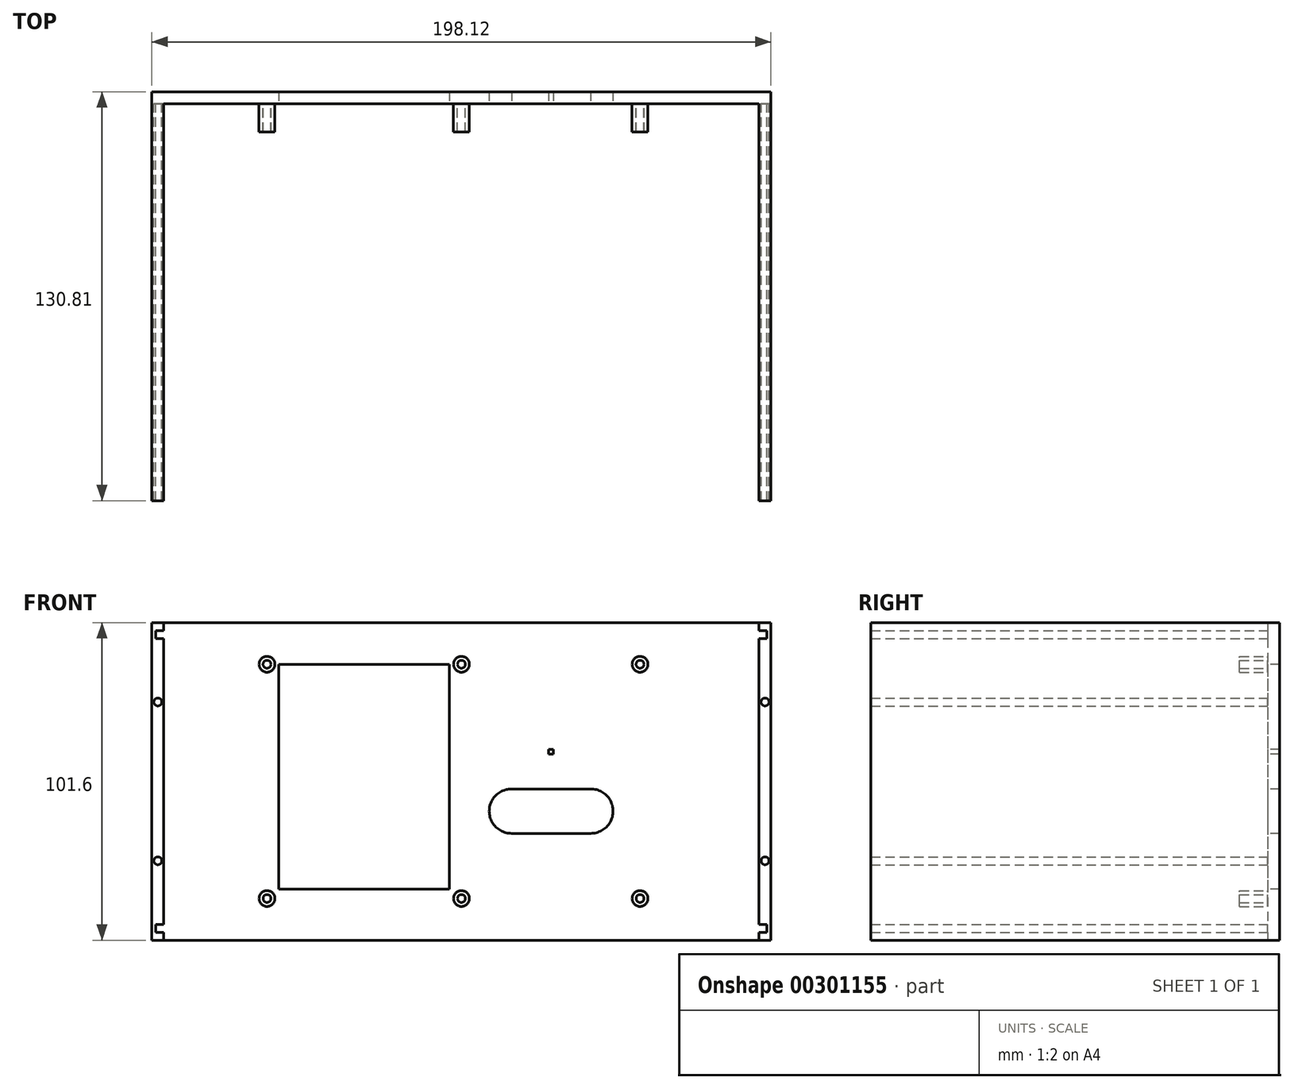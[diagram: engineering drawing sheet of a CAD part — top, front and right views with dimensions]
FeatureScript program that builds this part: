
annotation { "Feature Type Name" : "Feature", "Feature Type Description" : "" }
export const myFeature = defineFeature(function(context is Context, id is Id, definition is map)
    precondition{}
    {
        {
            var Q0;
            Q0=qCreatedBy(makeId("Front.planeOp"),FACE);
            var sketch = newSketch(context, id + "F0", { "sketchPlane" : qUnion([Q0])});
            skLineSegment(sketch, "E0.bottom", {"start": v(99.06, 50.8) * mm, "end": v(-99.06, 50.8) * mm});
            skLineSegment(sketch, "E0.top", {"start": v(99.06, -50.8) * mm, "end": v(-99.06, -50.8) * mm});
            skLineSegment(sketch, "E0.left", {"start": v(99.06, 50.8) * mm, "end": v(99.06, -50.8) * mm});
            skLineSegment(sketch, "E0.right", {"start": v(-99.06, 50.8) * mm, "end": v(-99.06, -50.8) * mm});
            skPoint(sketch, "E0.middle", {"position": v(0, 0) * mm});
            skSolve(sketch);
        }
        {
            var Q0;
            Q0=qCreatedBy(makeId("Front.planeOp"),FACE);
            var sketch = newSketch(context, id + "F1", { "sketchPlane" : qUnion([Q0])});
            skCircle(sketch, "E1", {"center": v(-62.23, -37.47) * mm, "radius": 2.54 * mm});
            skCircle(sketch, "E2", {"center": v(-62.23, 37.47) * mm, "radius": 2.54 * mm});
            skCircle(sketch, "E3", {"center": v(0, 37.47) * mm, "radius": 2.54 * mm});
            skCircle(sketch, "E4", {"center": v(0, -37.46) * mm, "radius": 2.54 * mm});
            skCircle(sketch, "E5", {"center": v(57.15, -37.46) * mm, "radius": 2.54 * mm});
            skCircle(sketch, "E6", {"center": v(57.15, 37.47) * mm, "radius": 2.54 * mm});
            skSolve(sketch);
        }
        {
            var Q0;
            Q0 = qSketchRegion(id + "F0", true);
            extrude(context, id + "F2", {"entities" : qUnion([Q0]), "depth" : 3.8 * mm});
        }
        {
            var Q0;
            Q0 = qSketchRegion(id + "F1", true);
            extrude(context, id + "F3", {"entities" : qUnion([Q0]), "operationType" : NewBodyOperationType.ADD, "depth" : 12.88 * mm});
        }
        {
            var Q0;
            Q0=makeQuery(id+"F2.opExtrude","CAP_FACE",FACE,{"disambiguationData":[OSD([sQuery(id+"F0.wireOp",EDGE,"E0.bottom"),sQuery(id+"F0.wireOp",EDGE,"E0.top"),sQuery(id+"F0.wireOp",EDGE,"E0.left"),sQuery(id+"F0.wireOp",EDGE,"E0.right")])],"isStart":false});
            var sketch = newSketch(context, id + "F4", { "sketchPlane" : qUnion([Q0])});
            skCircle(sketch, "E7", {"center": v(-62.23, 37.47) * mm, "radius": 1.27 * mm});
            skCircle(sketch, "E8", {"center": v(-62.23, -37.47) * mm, "radius": 1.26 * mm});
            skCircle(sketch, "E9", {"center": v(57.15, -37.46) * mm, "radius": 1.27 * mm});
            skCircle(sketch, "E10", {"center": v(57.15, 37.47) * mm, "radius": 1.27 * mm});
            skCircle(sketch, "E11", {"center": v(0, -37.46) * mm, "radius": 1.27 * mm});
            skCircle(sketch, "E12", {"center": v(0, 37.47) * mm, "radius": 1.26 * mm});
            skSolve(sketch);
        }
        {
            var Q0;
            Q0 = qSketchRegion(id + "F4", true);
            extrude(context, id + "F5", {"entities" : qUnion([Q0]), "operationType" : NewBodyOperationType.REMOVE, "depth" : 10.34 * mm});
        }
        {
            var Q0;
            Q0=makeQuery(id+"F2.opExtrude","CAP_FACE",FACE,{"disambiguationData":[OSD([sQuery(id+"F0.wireOp",EDGE,"E0.bottom"),sQuery(id+"F0.wireOp",EDGE,"E0.top"),sQuery(id+"F0.wireOp",EDGE,"E0.left"),sQuery(id+"F0.wireOp",EDGE,"E0.right")])],"isStart":false});
            var sketch = newSketch(context, id + "F6", { "sketchPlane" : qUnion([Q0])});
            skLineSegment(sketch, "E13.bottom", {"start": v(-58.42, 37.47) * mm, "end": v(-3.81, 37.47) * mm});
            skLineSegment(sketch, "E13.top", {"start": v(-58.42, -34.42) * mm, "end": v(-3.8, -34.42) * mm});
            skLineSegment(sketch, "E13.left", {"start": v(-58.42, 37.47) * mm, "end": v(-58.42, -34.42) * mm});
            skLineSegment(sketch, "E13.right", {"start": v(-3.81, 37.47) * mm, "end": v(-3.8, -34.42) * mm});
            skCircle(sketch, "E14", {"center": v(16, -9.52) * mm, "radius": 7.11 * mm});
            skCircle(sketch, "E15", {"center": v(41.4, -9.52) * mm, "radius": 7.11 * mm});
            skLineSegment(sketch, "E16.bottom", {"start": v(15.95, -2.41) * mm, "end": v(41.32, -2.41) * mm});
            skLineSegment(sketch, "E16.top", {"start": v(15.95, -16.64) * mm, "end": v(41.32, -16.64) * mm});
            skLineSegment(sketch, "E16.left", {"start": v(15.95, -2.41) * mm, "end": v(15.95, -16.64) * mm});
            skLineSegment(sketch, "E16.right", {"start": v(41.32, -2.41) * mm, "end": v(41.32, -16.64) * mm});
            skLineSegment(sketch, "E17.bottom", {"start": v(27.94, 10.29) * mm, "end": v(29.46, 10.29) * mm});
            skLineSegment(sketch, "E17.top", {"start": v(27.94, 8.76) * mm, "end": v(29.46, 8.76) * mm});
            skLineSegment(sketch, "E17.left", {"start": v(27.94, 10.29) * mm, "end": v(27.94, 8.76) * mm});
            skLineSegment(sketch, "E17.right", {"start": v(29.46, 10.29) * mm, "end": v(29.46, 8.76) * mm});
            skSolve(sketch);
        }
        {
            var Q0;
            Q0=makeQuery(id+"F6.imprint","IMPRINT",FACE,{"disambiguationData":[TD([[makeQuery(id+"F6.imprint","IMPRINT",EDGE,{"derivedFrom":sQuery(id+"F6.wireOp",EDGE,"E13.bottom")}),-1.0]])]});
            var Q1;
            Q1=makeQuery(id+"F6.imprint","IMPRINT",FACE,{"disambiguationData":[TD([[makeQuery(id+"F6.imprint","IMPRINT",EDGE,{"derivedFrom":sQuery(id+"F6.wireOp",EDGE,"E14")}),1.0]])]});
            var Q2;
            Q2=makeQuery(id+"F6.imprint","IMPRINT",FACE,{"disambiguationData":[TD([[makeQuery(id+"F6.imprint","IMPRINT",EDGE,{"derivedFrom":sQuery(id+"F6.wireOp",EDGE,"E15")}),1.0]])]});
            var Q3;
            {var subQ1=sQuery(id+"F6.wireOp",EDGE,"E16.bottom");var subQ3=sQuery(id+"F6.wireOp",EDGE,"E14");var subQ4=makeQuery(id+"F6.imprint","INTERSECT",VERTEX,{"derivedFrom":[subQ3,subQ1]});Q3=makeQuery(id+"F6.imprint","IMPRINT",FACE,{"disambiguationData":[TD([[makeQuery(id+"F6.imprint","IMPRINT",EDGE,{"disambiguationData":[TD([[subQ4,1.0]])],"derivedFrom":subQ3}),-1.0]])]});}
            var Q4;
            {var subQ5=sQuery(id+"F6.wireOp",EDGE,"E16.left");Q4=makeQuery(id+"F6.imprint","IMPRINT",FACE,{"disambiguationData":[TD([[makeQuery(id+"F6.imprint","IMPRINT",EDGE,{"derivedFrom":subQ5}),1.0]])]});}
            var Q5;
            {var subQ0=sQuery(id+"F6.wireOp",EDGE,"E16.left");Q5=makeQuery(id+"F6.imprint","IMPRINT",FACE,{"disambiguationData":[TD([[makeQuery(id+"F6.imprint","IMPRINT",EDGE,{"derivedFrom":subQ0}),-1.0]])]});}
            var Q6;
            Q6=makeQuery(id+"F6.imprint","IMPRINT",FACE,{"disambiguationData":[TD([[makeQuery(id+"F6.imprint","IMPRINT",EDGE,{"derivedFrom":sQuery(id+"F6.wireOp",EDGE,"E17.bottom")}),-1.0]])]});
            extrude(context, id + "F7", {"entities" : qUnion([Q0, Q1, Q2, Q3, Q4, Q5, Q6]), "operationType" : NewBodyOperationType.REMOVE, "oppositeDirection" : true, "depth" : 3.8 * mm});
        }
        {
            var Q0;
            Q0=makeQuery(id+"F2.opExtrude","CAP_FACE",FACE,{"disambiguationData":[OSD([sQuery(id+"F0.wireOp",EDGE,"E0.bottom"),sQuery(id+"F0.wireOp",EDGE,"E0.top"),sQuery(id+"F0.wireOp",EDGE,"E0.left"),sQuery(id+"F0.wireOp",EDGE,"E0.right")])],"isStart":false});
            var sketch = newSketch(context, id + "F8", { "sketchPlane" : qUnion([Q0])});
            skLineSegment(sketch, "E18.bottom", {"start": v(-99.06, 50.8) * mm, "end": v(-95.25, 50.8) * mm});
            skLineSegment(sketch, "E18.top", {"start": v(-99.06, -50.8) * mm, "end": v(-95.25, -50.8) * mm});
            skLineSegment(sketch, "E18.left", {"start": v(-99.06, 50.8) * mm, "end": v(-99.06, -50.8) * mm});
            skLineSegment(sketch, "E18.right", {"start": v(-95.25, 50.8) * mm, "end": v(-95.25, -50.8) * mm});
            skLineSegment(sketch, "E19.bottom", {"start": v(99.06, 50.8) * mm, "end": v(95.25, 50.8) * mm});
            skLineSegment(sketch, "E19.top", {"start": v(99.06, -50.8) * mm, "end": v(95.25, -50.8) * mm});
            skLineSegment(sketch, "E19.left", {"start": v(99.06, 50.8) * mm, "end": v(99.06, -50.8) * mm});
            skLineSegment(sketch, "E19.right", {"start": v(95.25, 50.8) * mm, "end": v(95.25, -50.8) * mm});
            skSolve(sketch);
        }
        {
            var Q0;
            Q0 = qSketchRegion(id + "F8", true);
            extrude(context, id + "F9", {"entities" : qUnion([Q0]), "operationType" : NewBodyOperationType.ADD, "depth" : 127 * mm});
        }
        {
            var Q0;
            Q0=makeQuery(id+"F2.opExtrude","CAP_FACE",FACE,{"disambiguationData":[OSD([sQuery(id+"F0.wireOp",EDGE,"E0.bottom"),sQuery(id+"F0.wireOp",EDGE,"E0.top"),sQuery(id+"F0.wireOp",EDGE,"E0.left"),sQuery(id+"F0.wireOp",EDGE,"E0.right")])],"isStart":false});
            var sketch = newSketch(context, id + "F10", { "sketchPlane" : qUnion([Q0])});
            skLineSegment(sketch, "E20.bottom", {"start": v(-95.25, 48.26) * mm, "end": v(-97.8, 48.26) * mm});
            skLineSegment(sketch, "E20.top", {"start": v(-95.25, 45.72) * mm, "end": v(-97.8, 45.72) * mm});
            skLineSegment(sketch, "E20.left", {"start": v(-95.25, 48.26) * mm, "end": v(-95.25, 45.72) * mm});
            skLineSegment(sketch, "E20.right", {"start": v(-97.8, 48.26) * mm, "end": v(-97.8, 45.72) * mm});
            skLineSegment(sketch, "E21.bottom", {"start": v(-95.25, -48.26) * mm, "end": v(-97.8, -48.26) * mm});
            skLineSegment(sketch, "E21.top", {"start": v(-95.25, -45.7) * mm, "end": v(-97.8, -45.7) * mm});
            skLineSegment(sketch, "E21.left", {"start": v(-95.25, -48.26) * mm, "end": v(-95.25, -45.7) * mm});
            skLineSegment(sketch, "E21.right", {"start": v(-97.8, -48.26) * mm, "end": v(-97.8, -45.7) * mm});
            skLineSegment(sketch, "E22.bottom", {"start": v(95.25, 48.26) * mm, "end": v(97.8, 48.26) * mm});
            skLineSegment(sketch, "E22.top", {"start": v(95.25, 45.72) * mm, "end": v(97.8, 45.72) * mm});
            skLineSegment(sketch, "E22.left", {"start": v(95.25, 48.26) * mm, "end": v(95.25, 45.72) * mm});
            skLineSegment(sketch, "E22.right", {"start": v(97.8, 48.26) * mm, "end": v(97.8, 45.72) * mm});
            skLineSegment(sketch, "E23.bottom", {"start": v(95.25, -48.26) * mm, "end": v(97.8, -48.26) * mm});
            skLineSegment(sketch, "E23.top", {"start": v(95.25, -45.72) * mm, "end": v(97.8, -45.72) * mm});
            skLineSegment(sketch, "E23.left", {"start": v(95.25, -48.26) * mm, "end": v(95.25, -45.72) * mm});
            skLineSegment(sketch, "E23.right", {"start": v(97.8, -48.26) * mm, "end": v(97.8, -45.72) * mm});
            skCircle(sketch, "E24", {"center": v(97.16, -25.4) * mm, "radius": 1.27 * mm});
            skCircle(sketch, "E25", {"center": v(97.16, 25.4) * mm, "radius": 1.28 * mm});
            skCircle(sketch, "E26", {"center": v(-97.16, 25.4) * mm, "radius": 1.27 * mm});
            skCircle(sketch, "E27", {"center": v(-97.16, -25.4) * mm, "radius": 1.27 * mm});
            skSolve(sketch);
        }
        {
            var Q0;
            Q0 = qSketchRegion(id + "F10", true);
            extrude(context, id + "F11", {"entities" : qUnion([Q0]), "operationType" : NewBodyOperationType.REMOVE, "depth" : 127 * mm});
        }
    });
